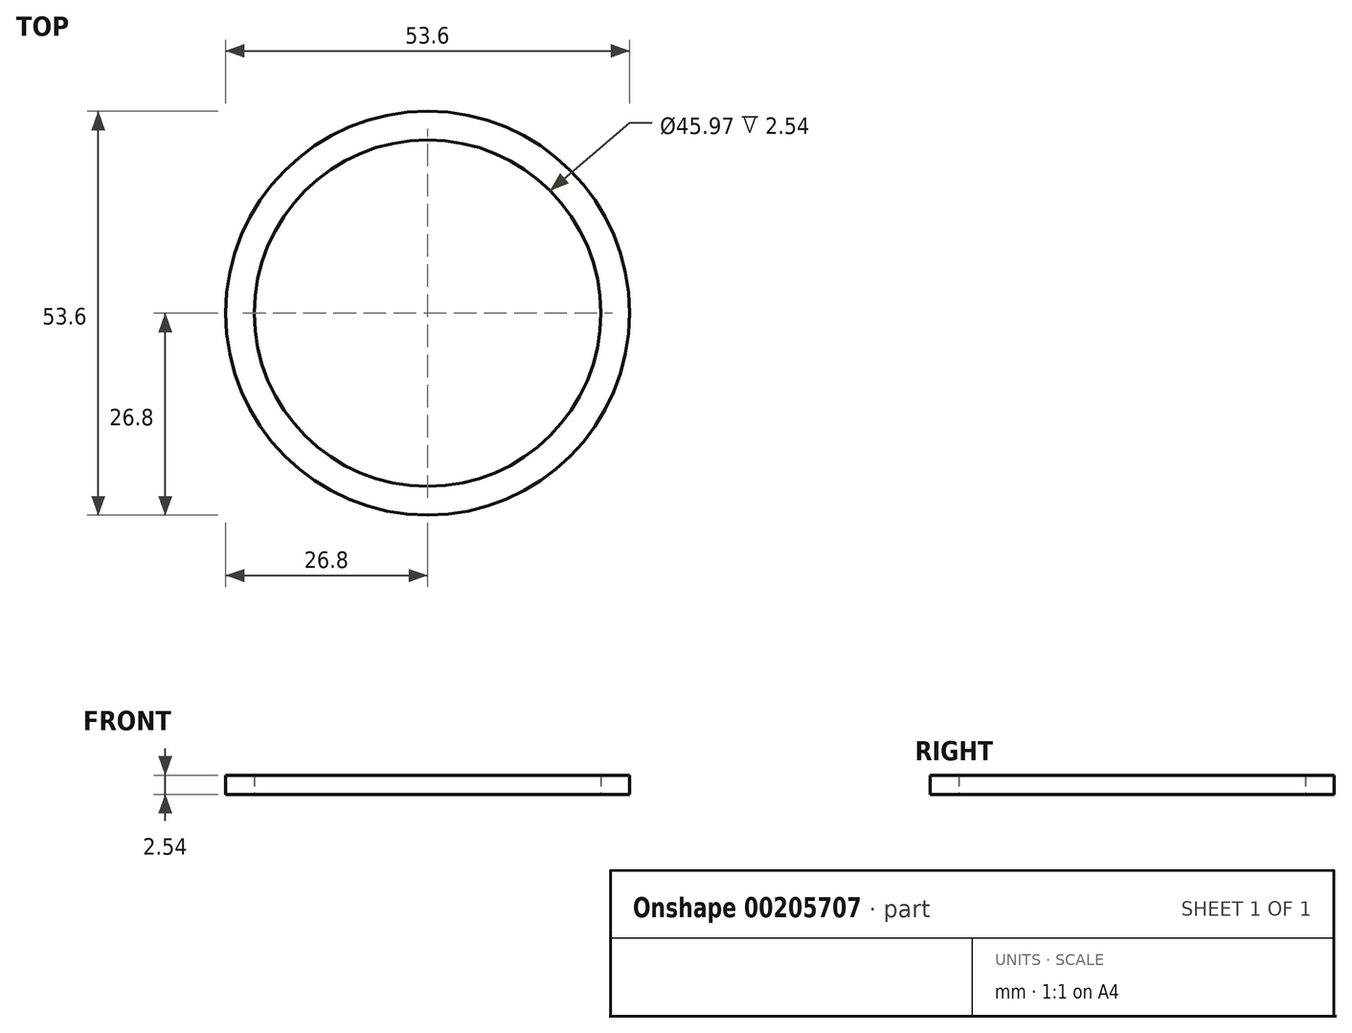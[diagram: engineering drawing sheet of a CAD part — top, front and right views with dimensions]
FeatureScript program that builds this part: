
annotation { "Feature Type Name" : "Feature", "Feature Type Description" : "" }
export const myFeature = defineFeature(function(context is Context, id is Id, definition is map)
    precondition{}
    {
        {
            var Q0;
            Q0=qCreatedBy(makeId("Top.planeOp"),FACE);
            var sketch = newSketch(context, id + "F0", { "sketchPlane" : qUnion([Q0])});
            skCircle(sketch, "E0", {"center": v(0, 0) * mm, "radius": 26.8 * mm});
            skCircle(sketch, "E1", {"center": v(0, 0) * mm, "radius": 22.99 * mm});
            skSolve(sketch);
        }
        {
            var Q0;
            Q0 = qSketchRegion(id + "F0", true);
            extrude(context, id + "F1", {"entities" : qUnion([Q0]), "depth" : 2.54 * mm});
        }
    });
